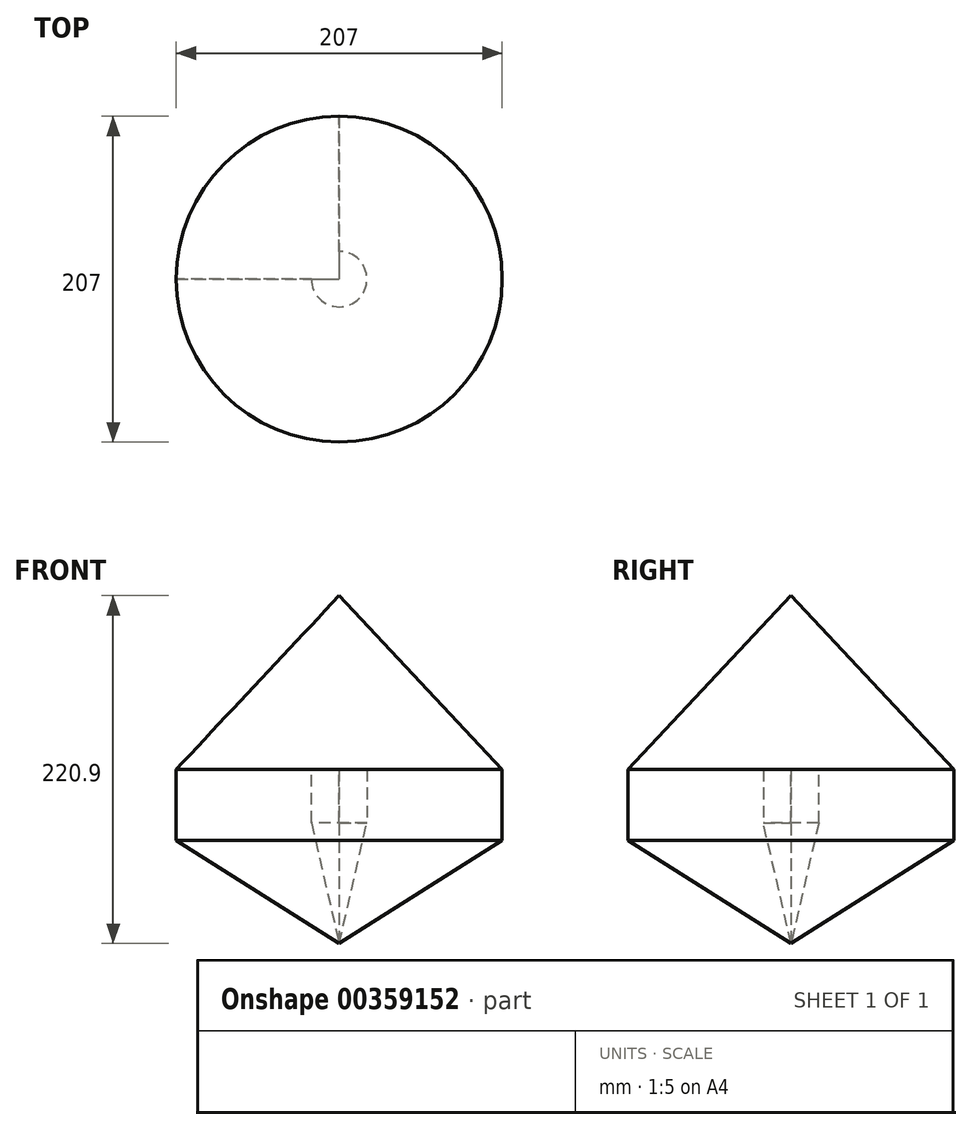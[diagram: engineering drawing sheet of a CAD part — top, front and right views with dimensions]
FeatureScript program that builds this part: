
annotation { "Feature Type Name" : "Feature", "Feature Type Description" : "" }
export const myFeature = defineFeature(function(context is Context, id is Id, definition is map)
    precondition{}
    {
        {
            var Q0;
            Q0=qCreatedBy(makeId("Top.planeOp"),FACE);
            var sketch = newSketch(context, id + "F0", { "sketchPlane" : qUnion([Q0])});
            skCircle(sketch, "E0", {"center": v(0, 0) * mm, "radius": 45 * mm});
            skSolve(sketch);
        }
        {
            var Q0;
            Q0=makeQuery(id+"F0.imprint","IMPRINT",FACE,{"disambiguationData":[TD([[makeQuery(id+"F0.imprint","IMPRINT",EDGE,{"derivedFrom":sQuery(id+"F0.wireOp",EDGE,"E0")}),1.0]])]});
            var sketch = newSketch(context, id + "F1", { "sketchPlane" : qUnion([Q0])});
            skCircle(sketch, "E1", {"center": v(0, 0) * mm, "radius": 103.5 * mm});
            skSolve(sketch);
        }
        {
            var Q0;
            Q0=qCreatedBy(makeId("Front.planeOp"),FACE);
            var sketch = newSketch(context, id + "F2", { "sketchPlane" : qUnion([Q0])});
            skLineSegment(sketch, "E2", {"start": v(0, 0) * mm, "end": v(-103.5, 0) * mm});
            skLineSegment(sketch, "E3", {"start": v(-103.5, 0) * mm, "end": v(0, 110.45) * mm});
            skLineSegment(sketch, "E4.0", {"start": v(-103.5, 0) * mm, "end": v(0, 0) * mm});
            skLineSegment(sketch, "E5", {"start": v(0, 110.45) * mm, "end": v(0, 0) * mm});
            skPoint(sketch, "E6.orphan", {"position": v(103.5, 0) * mm});
            skSolve(sketch);
        }
        {
            var Q0;
            Q0=makeQuery(id+"F2.imprint","IMPRINT",FACE,{"disambiguationData":[TD([[makeQuery(id+"F2.imprint","IMPRINT",EDGE,{"derivedFrom":sQuery(id+"F2.wireOp",EDGE,"E3")}),-1.0]])]});
            var Q1;
            Q1=sQuery(id+"F1.wireOp",EDGE,"E1");
            revolve(context, id + "F3", {"entities" : qUnion([Q0]), "axis" : qUnion([Q1]), "revolveType" : RevolveType.FULL});
        }
        {
            var Q0;
            Q0=qCreatedBy(makeId("Front.planeOp"),FACE);
            var sketch = newSketch(context, id + "F4", { "sketchPlane" : qUnion([Q0])});
            skLineSegment(sketch, "E7", {"start": v(-103.5, 0) * mm, "end": v(-103.5, -45.07) * mm});
            skLineSegment(sketch, "E8", {"start": v(-17.63, -33.86) * mm, "end": v(-17.63, 0) * mm});
            skLineSegment(sketch, "E9", {"start": v(-17.63, 0) * mm, "end": v(-103.5, 0) * mm});
            skLineSegment(sketch, "E10", {"start": v(0, 0) * mm, "end": v(0, -110.45) * mm, "construction": true});
            skLineSegment(sketch, "E11", {"start": v(-17.63, -33.86) * mm, "end": v(0, -110.45) * mm});
            skLineSegment(sketch, "E12", {"start": v(-103.5, -45.07) * mm, "end": v(0, -110.45) * mm});
            skSolve(sketch);
        }
        {
            var Q0;
            Q0=makeQuery(id+"F4.imprint","IMPRINT",FACE,{"disambiguationData":[TD([[makeQuery(id+"F4.imprint","IMPRINT",EDGE,{"derivedFrom":sQuery(id+"F4.wireOp",EDGE,"E7")}),1.0]])]});
            var Q1;
            Q1=makeQuery(id+"F3.opRevolve","SWEPT_EDGE",EDGE,{"disambiguationData":[OSD([sQuery(id+"F2.wireOp",EDGE,"E3"),sQuery(id+"F2.wireOp",EDGE,"E4.0")])]});
            revolve(context, id + "F5", {"operationType" : NewBodyOperationType.ADD, "entities" : qUnion([Q0]), "axis" : qUnion([Q1]), "revolveType" : RevolveType.ONE_DIRECTION, "oppositeDirection" : true, "angle" : 270 * degree});
        }
    });
